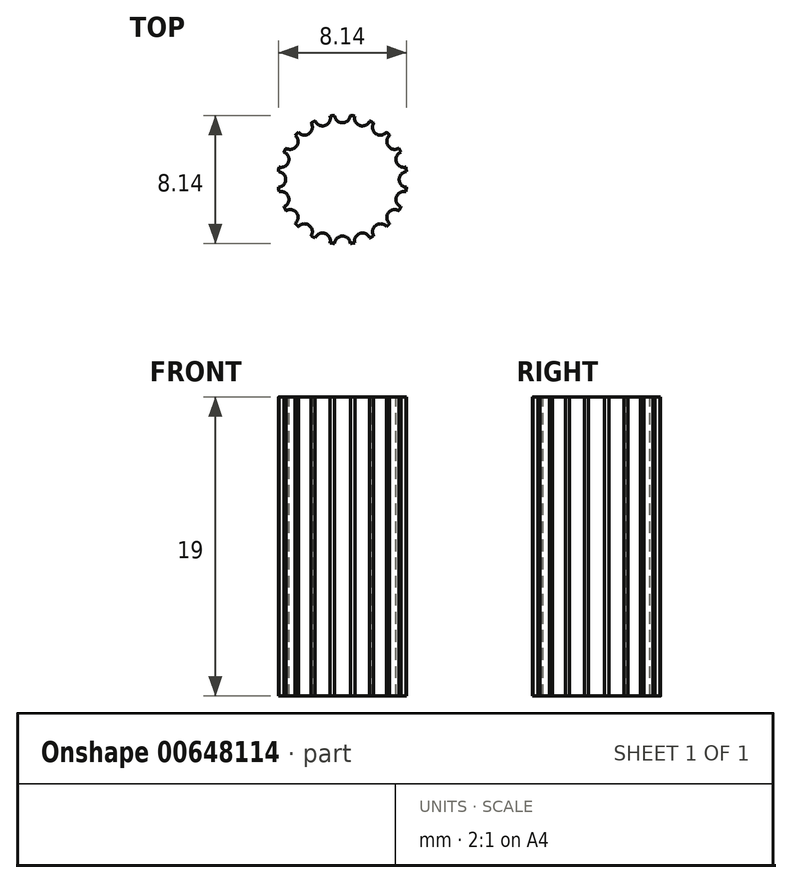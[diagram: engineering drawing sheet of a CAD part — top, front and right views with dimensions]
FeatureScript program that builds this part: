
annotation { "Feature Type Name" : "Feature", "Feature Type Description" : "" }
export const myFeature = defineFeature(function(context is Context, id is Id, definition is map)
    precondition{}
    {
        {
            var Q0;
            Q0=qCreatedBy(makeId("Top.planeOp"),FACE);
            var sketch = newSketch(context, id + "F0", { "sketchPlane" : qUnion([Q0])});
            skCircle(sketch, "E0", {"center": v(0, 0) * mm, "radius": 4.1 * mm});
            skCircle(sketch, "E1", {"center": v(0, 0) * mm, "radius": 3 * mm});
            skSolve(sketch);
        }
        {
            var Q0;
            Q0=makeQuery(id+"F0.imprint","IMPRINT",FACE,{"disambiguationData":[TD([[makeQuery(id+"F0.imprint","IMPRINT",EDGE,{"derivedFrom":sQuery(id+"F0.wireOp",EDGE,"E0")}),1.0]])]});
            var Q1;
            Q1=makeQuery(id+"F0.imprint","IMPRINT",FACE,{"disambiguationData":[TD([[makeQuery(id+"F0.imprint","IMPRINT",EDGE,{"derivedFrom":sQuery(id+"F0.wireOp",EDGE,"E1")}),1.0]])]});
            extrude(context, id + "F1", {"entities" : qUnion([Q0, Q1]), "depth" : 19 * mm, "offsetDistance" : 25 * mm});
        }
        {
            var Q0;
            Q0=makeQuery(id+"F1.opExtrude","CAP_FACE",FACE,{"disambiguationData":[OSD([sQuery(id+"F0.wireOp",EDGE,"E0")])],"isStart":false});
            var sketch = newSketch(context, id + "F2", { "sketchPlane" : qUnion([Q0])});
            skCircle(sketch, "E2", {"center": v(0, 4.1) * mm, "radius": 0.5 * mm});
            skCircle(sketch, "E3.1.0", {"center": v(-1.27, 3.9) * mm, "radius": 0.5 * mm});
            skCircle(sketch, "E3.2.0", {"center": v(-2.4, 3.32) * mm, "radius": 0.5 * mm});
            skCircle(sketch, "E3.3.0", {"center": v(-3.32, 2.4) * mm, "radius": 0.5 * mm});
            skCircle(sketch, "E3.4.0", {"center": v(-3.9, 1.27) * mm, "radius": 0.5 * mm});
            skCircle(sketch, "E3.5.0", {"center": v(-4.1, 0) * mm, "radius": 0.5 * mm});
            skCircle(sketch, "E3.6.0", {"center": v(-3.9, -1.27) * mm, "radius": 0.5 * mm});
            skCircle(sketch, "E3.7.0", {"center": v(-3.32, -2.4) * mm, "radius": 0.5 * mm});
            skCircle(sketch, "E3.8.0", {"center": v(-2.4, -3.32) * mm, "radius": 0.5 * mm});
            skCircle(sketch, "E3.9.0", {"center": v(-1.27, -3.9) * mm, "radius": 0.5 * mm});
            skCircle(sketch, "E3.10.0", {"center": v(0, -4.1) * mm, "radius": 0.5 * mm});
            skCircle(sketch, "E3.11.0", {"center": v(1.27, -3.9) * mm, "radius": 0.5 * mm});
            skCircle(sketch, "E3.12.0", {"center": v(2.4, -3.32) * mm, "radius": 0.5 * mm});
            skCircle(sketch, "E3.13.0", {"center": v(3.32, -2.4) * mm, "radius": 0.5 * mm});
            skCircle(sketch, "E3.14.0", {"center": v(3.9, -1.27) * mm, "radius": 0.5 * mm});
            skCircle(sketch, "E3.15.0", {"center": v(4.1, 0) * mm, "radius": 0.5 * mm});
            skCircle(sketch, "E3.16.0", {"center": v(3.9, 1.27) * mm, "radius": 0.5 * mm});
            skCircle(sketch, "E3.17.0", {"center": v(3.32, 2.4) * mm, "radius": 0.5 * mm});
            skCircle(sketch, "E3.18.0", {"center": v(2.4, 3.32) * mm, "radius": 0.5 * mm});
            skCircle(sketch, "E3.19.0", {"center": v(1.27, 3.9) * mm, "radius": 0.5 * mm});
            skPoint(sketch, "E3.center", {"position": v(0, 0) * mm});
            skSolve(sketch);
        }
        {
            var Q0;
            {var subQ0=sQuery(id+"F2.wireOp",EDGE,"E3.19.0");var subQ1=makeQuery(id+"F1.opExtrude","CAP_EDGE",EDGE,{"disambiguationData":[OSD([sQuery(id+"F0.wireOp",EDGE,"E0")])],"isStart":false});var subQ2=makeQuery(id+"F2.imprint","INTERSECT",VERTEX,{"disambiguationData":[OD(0.0)],"derivedFrom":[subQ1,subQ0]});Q0=makeQuery(id+"F2.imprint","IMPRINT",FACE,{"disambiguationData":[TD([[makeQuery(id+"F2.imprint","IMPRINT",EDGE,{"disambiguationData":[TD([[subQ2,-1.0]])],"derivedFrom":subQ0}),1.0]])]});}
            var Q1;
            {var subQ0=sQuery(id+"F2.wireOp",EDGE,"E3.18.0");var subQ1=makeQuery(id+"F1.opExtrude","CAP_EDGE",EDGE,{"disambiguationData":[OSD([sQuery(id+"F0.wireOp",EDGE,"E0")])],"isStart":false});var subQ2=makeQuery(id+"F2.imprint","INTERSECT",VERTEX,{"disambiguationData":[OD(0.0)],"derivedFrom":[subQ1,subQ0]});Q1=makeQuery(id+"F2.imprint","IMPRINT",FACE,{"disambiguationData":[TD([[makeQuery(id+"F2.imprint","IMPRINT",EDGE,{"disambiguationData":[TD([[subQ2,-1.0]])],"derivedFrom":subQ0}),1.0]])]});}
            var Q2;
            {var subQ0=sQuery(id+"F2.wireOp",EDGE,"E3.17.0");var subQ1=makeQuery(id+"F1.opExtrude","CAP_EDGE",EDGE,{"disambiguationData":[OSD([sQuery(id+"F0.wireOp",EDGE,"E0")])],"isStart":false});var subQ2=makeQuery(id+"F2.imprint","INTERSECT",VERTEX,{"disambiguationData":[OD(0.0)],"derivedFrom":[subQ1,subQ0]});Q2=makeQuery(id+"F2.imprint","IMPRINT",FACE,{"disambiguationData":[TD([[makeQuery(id+"F2.imprint","IMPRINT",EDGE,{"disambiguationData":[TD([[subQ2,-1.0]])],"derivedFrom":subQ0}),1.0]])]});}
            var Q3;
            {var subQ0=sQuery(id+"F2.wireOp",EDGE,"E3.16.0");var subQ1=makeQuery(id+"F1.opExtrude","CAP_EDGE",EDGE,{"disambiguationData":[OSD([sQuery(id+"F0.wireOp",EDGE,"E0")])],"isStart":false});var subQ2=makeQuery(id+"F2.imprint","INTERSECT",VERTEX,{"disambiguationData":[OD(0.0)],"derivedFrom":[subQ1,subQ0]});Q3=makeQuery(id+"F2.imprint","IMPRINT",FACE,{"disambiguationData":[TD([[makeQuery(id+"F2.imprint","IMPRINT",EDGE,{"disambiguationData":[TD([[subQ2,1.0]])],"derivedFrom":subQ0}),1.0]])]});}
            var Q4;
            {var subQ0=sQuery(id+"F2.wireOp",EDGE,"E3.15.0");var subQ1=makeQuery(id+"F1.opExtrude","CAP_EDGE",EDGE,{"disambiguationData":[OSD([sQuery(id+"F0.wireOp",EDGE,"E0")])],"isStart":false});var subQ2=makeQuery(id+"F2.imprint","INTERSECT",VERTEX,{"disambiguationData":[OD(0.0)],"derivedFrom":[subQ1,subQ0]});Q4=makeQuery(id+"F2.imprint","IMPRINT",FACE,{"disambiguationData":[TD([[makeQuery(id+"F2.imprint","IMPRINT",EDGE,{"disambiguationData":[TD([[subQ2,1.0]])],"derivedFrom":subQ0}),1.0]])]});}
            var Q5;
            {var subQ0=sQuery(id+"F2.wireOp",EDGE,"E3.14.0");var subQ1=makeQuery(id+"F1.opExtrude","CAP_EDGE",EDGE,{"disambiguationData":[OSD([sQuery(id+"F0.wireOp",EDGE,"E0")])],"isStart":false});var subQ2=makeQuery(id+"F2.imprint","INTERSECT",VERTEX,{"disambiguationData":[OD(0.0)],"derivedFrom":[subQ1,subQ0]});Q5=makeQuery(id+"F2.imprint","IMPRINT",FACE,{"disambiguationData":[TD([[makeQuery(id+"F2.imprint","IMPRINT",EDGE,{"disambiguationData":[TD([[subQ2,1.0]])],"derivedFrom":subQ0}),1.0]])]});}
            var Q6;
            {var subQ0=sQuery(id+"F2.wireOp",EDGE,"E3.13.0");var subQ1=makeQuery(id+"F1.opExtrude","CAP_EDGE",EDGE,{"disambiguationData":[OSD([sQuery(id+"F0.wireOp",EDGE,"E0")])],"isStart":false});var subQ2=makeQuery(id+"F2.imprint","INTERSECT",VERTEX,{"disambiguationData":[OD(0.0)],"derivedFrom":[subQ1,subQ0]});Q6=makeQuery(id+"F2.imprint","IMPRINT",FACE,{"disambiguationData":[TD([[makeQuery(id+"F2.imprint","IMPRINT",EDGE,{"disambiguationData":[TD([[subQ2,1.0]])],"derivedFrom":subQ0}),1.0]])]});}
            var Q7;
            {var subQ0=sQuery(id+"F2.wireOp",EDGE,"E3.12.0");var subQ1=makeQuery(id+"F1.opExtrude","CAP_EDGE",EDGE,{"disambiguationData":[OSD([sQuery(id+"F0.wireOp",EDGE,"E0")])],"isStart":false});var subQ2=makeQuery(id+"F2.imprint","INTERSECT",VERTEX,{"disambiguationData":[OD(0.0)],"derivedFrom":[subQ1,subQ0]});Q7=makeQuery(id+"F2.imprint","IMPRINT",FACE,{"disambiguationData":[TD([[makeQuery(id+"F2.imprint","IMPRINT",EDGE,{"disambiguationData":[TD([[subQ2,1.0]])],"derivedFrom":subQ0}),1.0]])]});}
            var Q8;
            {var subQ0=sQuery(id+"F2.wireOp",EDGE,"E3.11.0");var subQ1=makeQuery(id+"F1.opExtrude","CAP_EDGE",EDGE,{"disambiguationData":[OSD([sQuery(id+"F0.wireOp",EDGE,"E0")])],"isStart":false});var subQ2=makeQuery(id+"F2.imprint","INTERSECT",VERTEX,{"disambiguationData":[OD(0.0)],"derivedFrom":[subQ1,subQ0]});Q8=makeQuery(id+"F2.imprint","IMPRINT",FACE,{"disambiguationData":[TD([[makeQuery(id+"F2.imprint","IMPRINT",EDGE,{"disambiguationData":[TD([[subQ2,1.0]])],"derivedFrom":subQ0}),1.0]])]});}
            var Q9;
            {var subQ0=sQuery(id+"F2.wireOp",EDGE,"E3.10.0");var subQ1=makeQuery(id+"F1.opExtrude","CAP_EDGE",EDGE,{"disambiguationData":[OSD([sQuery(id+"F0.wireOp",EDGE,"E0")])],"isStart":false});var subQ2=makeQuery(id+"F2.imprint","INTERSECT",VERTEX,{"disambiguationData":[OD(0.0)],"derivedFrom":[subQ1,subQ0]});Q9=makeQuery(id+"F2.imprint","IMPRINT",FACE,{"disambiguationData":[TD([[makeQuery(id+"F2.imprint","IMPRINT",EDGE,{"disambiguationData":[TD([[subQ2,1.0]])],"derivedFrom":subQ0}),1.0]])]});}
            var Q10;
            {var subQ0=sQuery(id+"F2.wireOp",EDGE,"E3.9.0");var subQ1=makeQuery(id+"F1.opExtrude","CAP_EDGE",EDGE,{"disambiguationData":[OSD([sQuery(id+"F0.wireOp",EDGE,"E0")])],"isStart":false});var subQ2=makeQuery(id+"F2.imprint","INTERSECT",VERTEX,{"disambiguationData":[OD(0.0)],"derivedFrom":[subQ1,subQ0]});Q10=makeQuery(id+"F2.imprint","IMPRINT",FACE,{"disambiguationData":[TD([[makeQuery(id+"F2.imprint","IMPRINT",EDGE,{"disambiguationData":[TD([[subQ2,1.0]])],"derivedFrom":subQ0}),1.0]])]});}
            var Q11;
            {var subQ0=sQuery(id+"F2.wireOp",EDGE,"E3.8.0");var subQ1=makeQuery(id+"F1.opExtrude","CAP_EDGE",EDGE,{"disambiguationData":[OSD([sQuery(id+"F0.wireOp",EDGE,"E0")])],"isStart":false});var subQ2=makeQuery(id+"F2.imprint","INTERSECT",VERTEX,{"disambiguationData":[OD(0.0)],"derivedFrom":[subQ1,subQ0]});Q11=makeQuery(id+"F2.imprint","IMPRINT",FACE,{"disambiguationData":[TD([[makeQuery(id+"F2.imprint","IMPRINT",EDGE,{"disambiguationData":[TD([[subQ2,1.0]])],"derivedFrom":subQ0}),1.0]])]});}
            var Q12;
            {var subQ0=sQuery(id+"F2.wireOp",EDGE,"E3.7.0");var subQ1=makeQuery(id+"F1.opExtrude","CAP_EDGE",EDGE,{"disambiguationData":[OSD([sQuery(id+"F0.wireOp",EDGE,"E0")])],"isStart":false});var subQ2=makeQuery(id+"F2.imprint","INTERSECT",VERTEX,{"disambiguationData":[OD(0.0)],"derivedFrom":[subQ1,subQ0]});Q12=makeQuery(id+"F2.imprint","IMPRINT",FACE,{"disambiguationData":[TD([[makeQuery(id+"F2.imprint","IMPRINT",EDGE,{"disambiguationData":[TD([[subQ2,1.0]])],"derivedFrom":subQ0}),1.0]])]});}
            var Q13;
            {var subQ0=sQuery(id+"F2.wireOp",EDGE,"E3.6.0");var subQ1=makeQuery(id+"F1.opExtrude","CAP_EDGE",EDGE,{"disambiguationData":[OSD([sQuery(id+"F0.wireOp",EDGE,"E0")])],"isStart":false});var subQ2=makeQuery(id+"F2.imprint","INTERSECT",VERTEX,{"disambiguationData":[OD(0.0)],"derivedFrom":[subQ1,subQ0]});Q13=makeQuery(id+"F2.imprint","IMPRINT",FACE,{"disambiguationData":[TD([[makeQuery(id+"F2.imprint","IMPRINT",EDGE,{"disambiguationData":[TD([[subQ2,-1.0]])],"derivedFrom":subQ0}),1.0]])]});}
            var Q14;
            {var subQ0=sQuery(id+"F2.wireOp",EDGE,"E3.5.0");var subQ1=makeQuery(id+"F1.opExtrude","CAP_EDGE",EDGE,{"disambiguationData":[OSD([sQuery(id+"F0.wireOp",EDGE,"E0")])],"isStart":false});var subQ2=makeQuery(id+"F2.imprint","INTERSECT",VERTEX,{"disambiguationData":[OD(0.0)],"derivedFrom":[subQ1,subQ0]});Q14=makeQuery(id+"F2.imprint","IMPRINT",FACE,{"disambiguationData":[TD([[makeQuery(id+"F2.imprint","IMPRINT",EDGE,{"disambiguationData":[TD([[subQ2,-1.0]])],"derivedFrom":subQ0}),1.0]])]});}
            var Q15;
            {var subQ0=sQuery(id+"F2.wireOp",EDGE,"E3.4.0");var subQ1=makeQuery(id+"F1.opExtrude","CAP_EDGE",EDGE,{"disambiguationData":[OSD([sQuery(id+"F0.wireOp",EDGE,"E0")])],"isStart":false});var subQ2=makeQuery(id+"F2.imprint","INTERSECT",VERTEX,{"disambiguationData":[OD(0.0)],"derivedFrom":[subQ1,subQ0]});Q15=makeQuery(id+"F2.imprint","IMPRINT",FACE,{"disambiguationData":[TD([[makeQuery(id+"F2.imprint","IMPRINT",EDGE,{"disambiguationData":[TD([[subQ2,-1.0]])],"derivedFrom":subQ0}),1.0]])]});}
            var Q16;
            {var subQ0=sQuery(id+"F2.wireOp",EDGE,"E3.3.0");var subQ1=makeQuery(id+"F1.opExtrude","CAP_EDGE",EDGE,{"disambiguationData":[OSD([sQuery(id+"F0.wireOp",EDGE,"E0")])],"isStart":false});var subQ2=makeQuery(id+"F2.imprint","INTERSECT",VERTEX,{"disambiguationData":[OD(0.0)],"derivedFrom":[subQ1,subQ0]});Q16=makeQuery(id+"F2.imprint","IMPRINT",FACE,{"disambiguationData":[TD([[makeQuery(id+"F2.imprint","IMPRINT",EDGE,{"disambiguationData":[TD([[subQ2,-1.0]])],"derivedFrom":subQ0}),1.0]])]});}
            var Q17;
            {var subQ0=sQuery(id+"F2.wireOp",EDGE,"E3.2.0");var subQ1=makeQuery(id+"F1.opExtrude","CAP_EDGE",EDGE,{"disambiguationData":[OSD([sQuery(id+"F0.wireOp",EDGE,"E0")])],"isStart":false});var subQ2=makeQuery(id+"F2.imprint","INTERSECT",VERTEX,{"disambiguationData":[OD(0.0)],"derivedFrom":[subQ1,subQ0]});Q17=makeQuery(id+"F2.imprint","IMPRINT",FACE,{"disambiguationData":[TD([[makeQuery(id+"F2.imprint","IMPRINT",EDGE,{"disambiguationData":[TD([[subQ2,-1.0]])],"derivedFrom":subQ0}),1.0]])]});}
            var Q18;
            {var subQ0=sQuery(id+"F2.wireOp",EDGE,"E3.1.0");var subQ1=makeQuery(id+"F1.opExtrude","CAP_EDGE",EDGE,{"disambiguationData":[OSD([sQuery(id+"F0.wireOp",EDGE,"E0")])],"isStart":false});var subQ2=makeQuery(id+"F2.imprint","INTERSECT",VERTEX,{"disambiguationData":[OD(0.0)],"derivedFrom":[subQ1,subQ0]});Q18=makeQuery(id+"F2.imprint","IMPRINT",FACE,{"disambiguationData":[TD([[makeQuery(id+"F2.imprint","IMPRINT",EDGE,{"disambiguationData":[TD([[subQ2,-1.0]])],"derivedFrom":subQ0}),1.0]])]});}
            var Q19;
            {var subQ0=sQuery(id+"F2.wireOp",EDGE,"E2");var subQ1=makeQuery(id+"F1.opExtrude","CAP_EDGE",EDGE,{"disambiguationData":[OSD([sQuery(id+"F0.wireOp",EDGE,"E0")])],"isStart":false});var subQ2=makeQuery(id+"F2.imprint","INTERSECT",VERTEX,{"disambiguationData":[OD(0.0)],"derivedFrom":[subQ1,subQ0]});Q19=makeQuery(id+"F2.imprint","IMPRINT",FACE,{"disambiguationData":[TD([[makeQuery(id+"F2.imprint","IMPRINT",EDGE,{"disambiguationData":[TD([[subQ2,-1.0]])],"derivedFrom":subQ0}),1.0]])]});}
            extrude(context, id + "F3", {"entities" : qUnion([Q0, Q1, Q2, Q3, Q4, Q5, Q6, Q7, Q8, Q9, Q10, Q11, Q12, Q13, Q14, Q15, Q16, Q17, Q18, Q19]), "operationType" : NewBodyOperationType.REMOVE, "oppositeDirection" : true, "depth" : 25 * mm, "offsetDistance" : 25 * mm});
        }
    });
